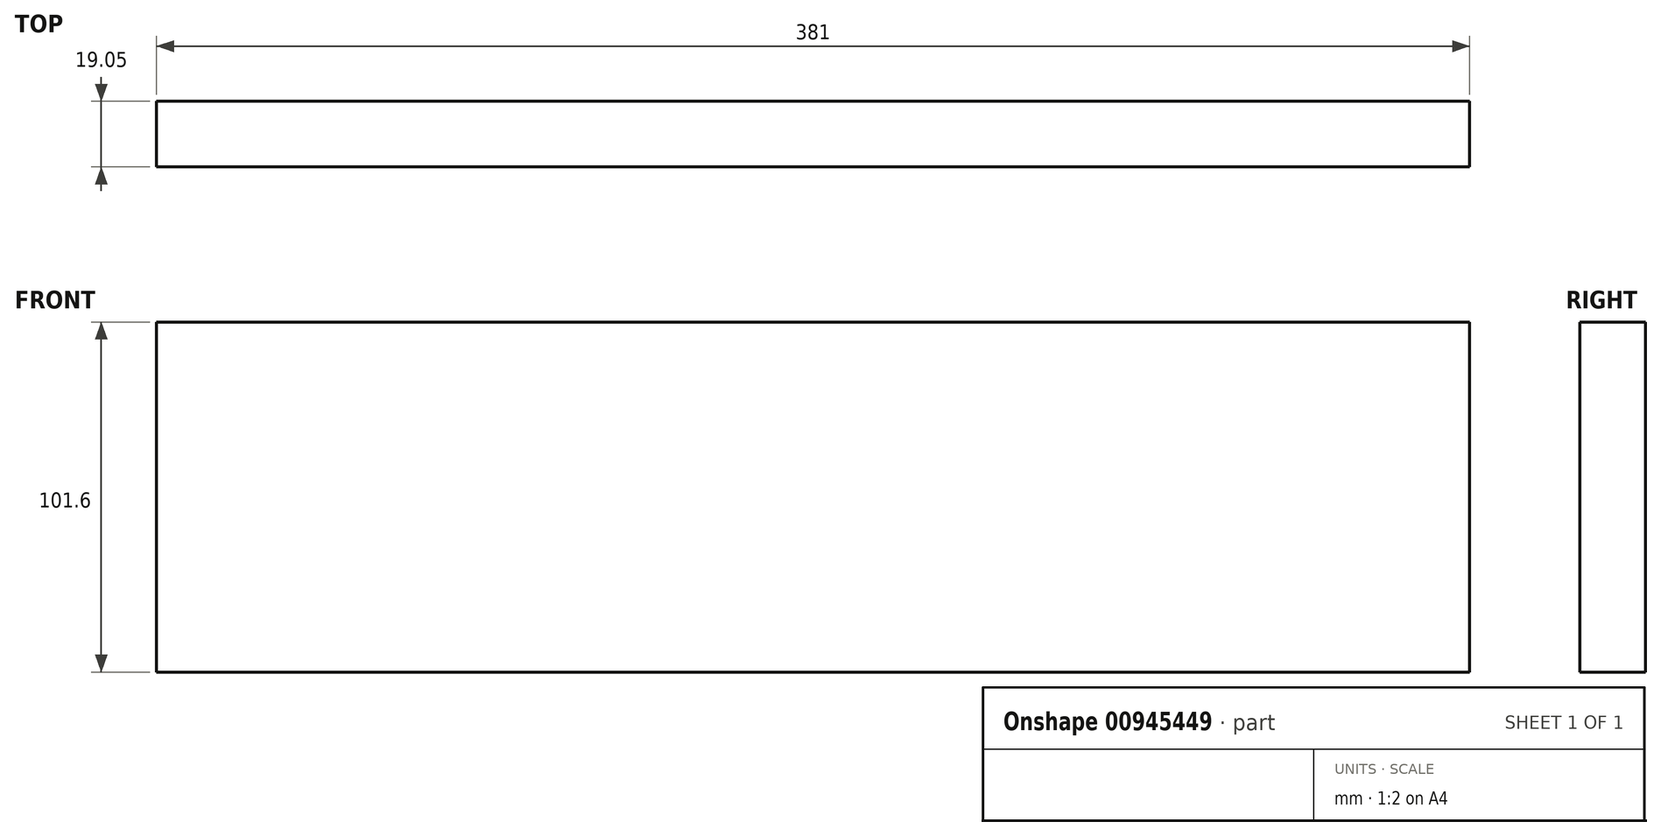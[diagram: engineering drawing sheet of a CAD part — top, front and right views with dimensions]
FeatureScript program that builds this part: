
annotation { "Feature Type Name" : "Feature", "Feature Type Description" : "" }
export const myFeature = defineFeature(function(context is Context, id is Id, definition is map)
    precondition{}
    {
        {
            var Q0;
            Q0=qCreatedBy(makeId("Front.planeOp"),FACE);
            var sketch = newSketch(context, id + "F0", { "sketchPlane" : qUnion([Q0])});
            skLineSegment(sketch, "E0.bottom", {"start": v(0, 0) * mm, "end": v(381, 0) * mm});
            skLineSegment(sketch, "E0.top", {"start": v(0, 101.6) * mm, "end": v(381, 101.6) * mm});
            skLineSegment(sketch, "E0.left", {"start": v(0, 0) * mm, "end": v(0, 101.6) * mm});
            skLineSegment(sketch, "E0.right", {"start": v(381, 0) * mm, "end": v(381, 101.6) * mm});
            skSolve(sketch);
        }
        {
            var Q0;
            Q0=makeQuery(id+"F0.imprint","IMPRINT",FACE,{"disambiguationData":[TD([[makeQuery(id+"F0.imprint","IMPRINT",EDGE,{"derivedFrom":sQuery(id+"F0.wireOp",EDGE,"E0.bottom")}),1.0]])]});
            extrude(context, id + "F1", {"entities" : qUnion([Q0]), "depth" : 19.05 * mm, "offsetDistance" : 25.4 * mm});
        }
    });
